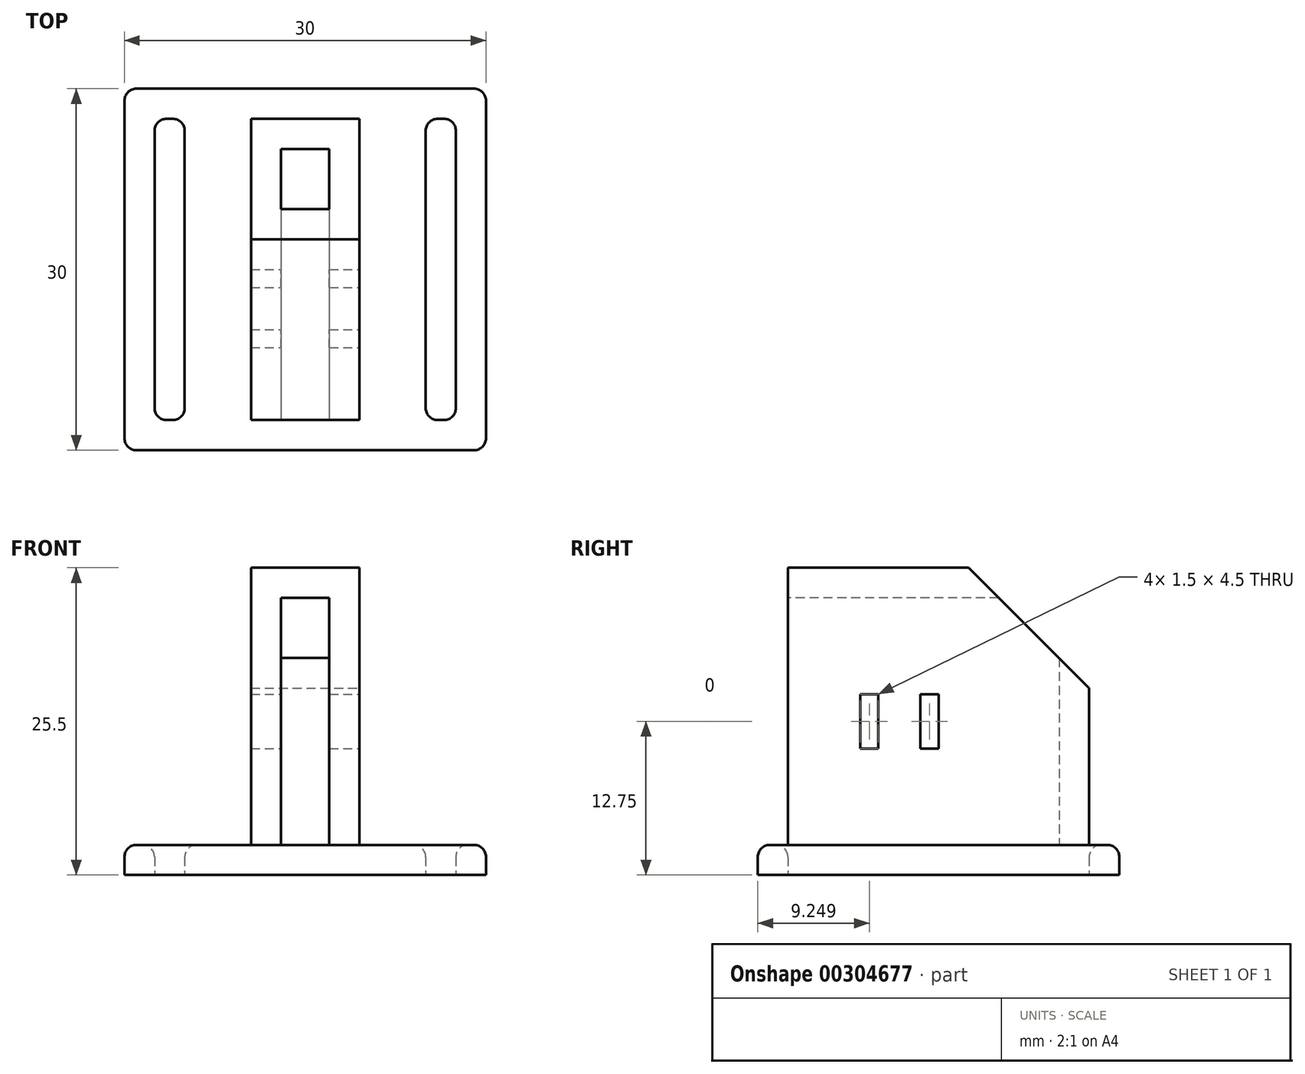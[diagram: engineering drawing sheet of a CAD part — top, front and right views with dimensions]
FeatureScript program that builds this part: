
annotation { "Feature Type Name" : "Feature", "Feature Type Description" : "" }
export const myFeature = defineFeature(function(context is Context, id is Id, definition is map)
    precondition{}
    {
        {
            var Q0;
            Q0=qCreatedBy(makeId("Top.planeOp"),FACE);
            var sketch = newSketch(context, id + "F0", { "sketchPlane" : qUnion([Q0])});
            skLineSegment(sketch, "E0.bottom", {"start": v(-52.92, 47.7) * mm, "end": v(-22.92, 47.7) * mm});
            skLineSegment(sketch, "E0.top", {"start": v(-52.92, 17.7) * mm, "end": v(-22.92, 17.7) * mm});
            skLineSegment(sketch, "E0.left", {"start": v(-52.92, 47.7) * mm, "end": v(-52.92, 17.7) * mm});
            skLineSegment(sketch, "E0.right", {"start": v(-22.92, 47.7) * mm, "end": v(-22.92, 17.7) * mm});
            skLineSegment(sketch, "E1.bottom", {"start": v(-50.42, 45.2) * mm, "end": v(-47.92, 45.2) * mm});
            skLineSegment(sketch, "E1.top", {"start": v(-50.42, 20.2) * mm, "end": v(-47.92, 20.2) * mm});
            skLineSegment(sketch, "E1.left", {"start": v(-50.42, 45.2) * mm, "end": v(-50.42, 20.2) * mm});
            skLineSegment(sketch, "E1.right", {"start": v(-47.92, 45.2) * mm, "end": v(-47.92, 20.2) * mm});
            skLineSegment(sketch, "E2.bottom", {"start": v(-25.42, 45.2) * mm, "end": v(-27.92, 45.2) * mm});
            skLineSegment(sketch, "E2.top", {"start": v(-25.42, 20.2) * mm, "end": v(-27.92, 20.2) * mm});
            skLineSegment(sketch, "E2.left", {"start": v(-25.42, 45.2) * mm, "end": v(-25.42, 20.2) * mm});
            skLineSegment(sketch, "E2.right", {"start": v(-27.92, 45.2) * mm, "end": v(-27.92, 20.2) * mm});
            skSolve(sketch);
        }
        {
            var Q0;
            Q0=makeQuery(id+"F0.imprint","IMPRINT",FACE,{"disambiguationData":[TD([[makeQuery(id+"F0.imprint","IMPRINT",EDGE,{"derivedFrom":sQuery(id+"F0.wireOp",EDGE,"E0.bottom")}),-1.0]])]});
            extrude(context, id + "F1", {"entities" : qUnion([Q0]), "depth" : 2.5 * mm});
        }
        {
            var Q0;
            Q0=makeQuery(id+"F1.opExtrude","CAP_FACE",FACE,{"disambiguationData":[OSD([sQuery(id+"F0.wireOp",EDGE,"E0.bottom"),sQuery(id+"F0.wireOp",EDGE,"E0.top"),sQuery(id+"F0.wireOp",EDGE,"E0.left"),sQuery(id+"F0.wireOp",EDGE,"E0.right"),sQuery(id+"F0.wireOp",EDGE,"E1.bottom"),sQuery(id+"F0.wireOp",EDGE,"E1.top"),sQuery(id+"F0.wireOp",EDGE,"E1.left"),sQuery(id+"F0.wireOp",EDGE,"E1.right"),sQuery(id+"F0.wireOp",EDGE,"E2.bottom"),sQuery(id+"F0.wireOp",EDGE,"E2.top"),sQuery(id+"F0.wireOp",EDGE,"E2.left"),sQuery(id+"F0.wireOp",EDGE,"E2.right")])],"isStart":false});
            var sketch = newSketch(context, id + "F2", { "sketchPlane" : qUnion([Q0])});
            skLineSegment(sketch, "E3.bottom", {"start": v(-33.42, 45.2) * mm, "end": v(-35.92, 45.2) * mm});
            skLineSegment(sketch, "E3.top", {"start": v(-33.42, 20.2) * mm, "end": v(-35.92, 20.2) * mm});
            skLineSegment(sketch, "E3.left", {"start": v(-33.42, 45.2) * mm, "end": v(-33.42, 20.2) * mm});
            skLineSegment(sketch, "E3.right", {"start": v(-35.92, 45.2) * mm, "end": v(-35.92, 20.2) * mm});
            skLineSegment(sketch, "E4.bottom", {"start": v(-42.42, 45.2) * mm, "end": v(-39.92, 45.2) * mm});
            skLineSegment(sketch, "E4.top", {"start": v(-42.42, 20.2) * mm, "end": v(-39.92, 20.2) * mm});
            skLineSegment(sketch, "E4.left", {"start": v(-42.42, 45.2) * mm, "end": v(-42.42, 20.2) * mm});
            skLineSegment(sketch, "E4.right", {"start": v(-39.92, 45.2) * mm, "end": v(-39.92, 20.2) * mm});
            skLineSegment(sketch, "E5.bottom", {"start": v(-39.92, 45.2) * mm, "end": v(-35.92, 45.2) * mm});
            skLineSegment(sketch, "E5.top", {"start": v(-39.92, 42.7) * mm, "end": v(-35.92, 42.7) * mm});
            skLineSegment(sketch, "E5.left", {"start": v(-39.92, 45.2) * mm, "end": v(-39.92, 42.7) * mm});
            skLineSegment(sketch, "E5.right", {"start": v(-35.92, 45.2) * mm, "end": v(-35.92, 42.7) * mm});
            skSolve(sketch);
        }
        {
            var Q0;
            Q0=makeQuery(id+"F2.imprint","IMPRINT",FACE,{"disambiguationData":[TD([[makeQuery(id+"F2.imprint","IMPRINT",EDGE,{"derivedFrom":sQuery(id+"F2.wireOp",EDGE,"E4.bottom")}),-1.0]])]});
            var Q1;
            Q1=makeQuery(id+"F2.imprint","IMPRINT",FACE,{"disambiguationData":[TD([[makeQuery(id+"F2.imprint","IMPRINT",EDGE,{"derivedFrom":sQuery(id+"F2.wireOp",EDGE,"E3.bottom")}),1.0]])]});
            var Q2;
            Q2=makeQuery(id+"F2.imprint","IMPRINT",FACE,{"disambiguationData":[TD([[makeQuery(id+"F2.imprint","IMPRINT",EDGE,{"derivedFrom":sQuery(id+"F2.wireOp",EDGE,"E5.bottom")}),-1.0]])]});
            extrude(context, id + "F3", {"entities" : qUnion([Q0, Q1, Q2]), "depth" : 20.5 * mm});
        }
        {
            var Q0;
            Q0=makeQuery(id+"F3.opExtrude","CAP_FACE",FACE,{"disambiguationData":[OSD([sQuery(id+"F2.wireOp",EDGE,"E3.bottom"),sQuery(id+"F2.wireOp",EDGE,"E3.top"),sQuery(id+"F2.wireOp",EDGE,"E3.left"),sQuery(id+"F2.wireOp",EDGE,"E3.right"),sQuery(id+"F2.wireOp",EDGE,"E4.bottom"),sQuery(id+"F2.wireOp",EDGE,"E4.top"),sQuery(id+"F2.wireOp",EDGE,"E4.left"),sQuery(id+"F2.wireOp",EDGE,"E4.right"),sQuery(id+"F2.wireOp",EDGE,"E5.bottom"),sQuery(id+"F2.wireOp",EDGE,"E5.top")])],"isStart":false});
            var sketch = newSketch(context, id + "F4", { "sketchPlane" : qUnion([Q0])});
            skLineSegment(sketch, "E6.bottom", {"start": v(-42.42, 20.2) * mm, "end": v(-33.42, 20.2) * mm});
            skLineSegment(sketch, "E6.top", {"start": v(-42.42, 45.2) * mm, "end": v(-33.42, 45.2) * mm});
            skLineSegment(sketch, "E6.left", {"start": v(-42.42, 20.2) * mm, "end": v(-42.42, 45.2) * mm});
            skLineSegment(sketch, "E6.right", {"start": v(-33.42, 20.2) * mm, "end": v(-33.42, 45.2) * mm});
            skSolve(sketch);
        }
        {
            var Q0;
            Q0 = qSketchRegion(id + "F4", true);
            extrude(context, id + "F5", {"entities" : qUnion([Q0]), "operationType" : NewBodyOperationType.ADD, "depth" : 2.5 * mm});
        }
        {
            var Q0;
            Q0=makeQuery(id+"F5.boolean.opBoolean","MERGE",FACE,{"derivedFrom":[makeQuery(id+"F3.opExtrude","SWEPT_FACE",FACE,{"disambiguationData":[OSD([sQuery(id+"F2.wireOp",EDGE,"E3.left")])]}),makeQuery(id+"F5.opExtrude","SWEPT_FACE",FACE,{"disambiguationData":[OSD([sQuery(id+"F4.wireOp",EDGE,"E6.right")])]})]});
            var sketch = newSketch(context, id + "F6", { "sketchPlane" : qUnion([Q0])});
            skLineSegment(sketch, "E7.bottom", {"start": v(26.2, 15) * mm, "end": v(27.7, 15) * mm});
            skLineSegment(sketch, "E7.top", {"start": v(26.2, 10.5) * mm, "end": v(27.7, 10.5) * mm});
            skLineSegment(sketch, "E7.left", {"start": v(26.2, 15) * mm, "end": v(26.2, 10.5) * mm});
            skLineSegment(sketch, "E7.right", {"start": v(27.7, 15) * mm, "end": v(27.7, 10.5) * mm});
            skLineSegment(sketch, "E8.bottom", {"start": v(31.2, 15) * mm, "end": v(32.7, 15) * mm});
            skLineSegment(sketch, "E8.top", {"start": v(31.2, 10.5) * mm, "end": v(32.7, 10.5) * mm});
            skLineSegment(sketch, "E8.left", {"start": v(31.2, 15) * mm, "end": v(31.2, 10.5) * mm});
            skLineSegment(sketch, "E8.right", {"start": v(32.7, 15) * mm, "end": v(32.7, 10.5) * mm});
            skLineSegment(sketch, "E9", {"start": v(35.2, 25.5) * mm, "end": v(45.2, 15.5) * mm});
            skLineSegment(sketch, "E10", {"start": v(45.2, 15.5) * mm, "end": v(45.2, 25.5) * mm});
            skLineSegment(sketch, "E11", {"start": v(45.2, 25.5) * mm, "end": v(35.2, 25.5) * mm});
            skSolve(sketch);
        }
        {
            var Q0;
            Q0 = qSketchRegion(id + "F6", true);
            extrude(context, id + "F7", {"entities" : qUnion([Q0]), "operationType" : NewBodyOperationType.REMOVE, "oppositeDirection" : true, "depth" : 25 * mm});
        }
        {
            var Q0;
            Q0=makeQuery(id+"F1.opExtrude","SWEPT_EDGE",EDGE,{"disambiguationData":[OSD([sQuery(id+"F0.wireOp",EDGE,"E0.bottom"),sQuery(id+"F0.wireOp",EDGE,"E0.left")])]});
            var Q1;
            Q1=makeQuery(id+"F1.opExtrude","SWEPT_EDGE",EDGE,{"disambiguationData":[OSD([sQuery(id+"F0.wireOp",EDGE,"E0.top"),sQuery(id+"F0.wireOp",EDGE,"E0.left")])]});
            var Q2;
            Q2=makeQuery(id+"F3.opExtrude","SWEPT_EDGE",EDGE,{"disambiguationData":[OSD([sQuery(id+"F2.wireOp",EDGE,"E4.bottom"),sQuery(id+"F2.wireOp",EDGE,"E4.left")])]});
            var Q3;
            Q3=makeQuery(id+"F3.opExtrude","SWEPT_EDGE",EDGE,{"disambiguationData":[OSD([sQuery(id+"F2.wireOp",EDGE,"E3.bottom"),sQuery(id+"F2.wireOp",EDGE,"E3.left")])]});
            var Q4;
            Q4=makeQuery(id+"F1.opExtrude","SWEPT_EDGE",EDGE,{"disambiguationData":[OSD([sQuery(id+"F0.wireOp",EDGE,"E0.top"),sQuery(id+"F0.wireOp",EDGE,"E0.right")])]});
            var Q5;
            Q5=makeQuery(id+"F1.opExtrude","SWEPT_EDGE",EDGE,{"disambiguationData":[OSD([sQuery(id+"F0.wireOp",EDGE,"E0.bottom"),sQuery(id+"F0.wireOp",EDGE,"E0.right")])]});
            var Q6;
            Q6=makeQuery(id+"F1.opExtrude","SWEPT_EDGE",EDGE,{"disambiguationData":[OSD([sQuery(id+"F0.wireOp",EDGE,"E2.bottom"),sQuery(id+"F0.wireOp",EDGE,"E2.right")])]});
            var Q7;
            Q7=makeQuery(id+"F1.opExtrude","SWEPT_EDGE",EDGE,{"disambiguationData":[OSD([sQuery(id+"F0.wireOp",EDGE,"E1.bottom"),sQuery(id+"F0.wireOp",EDGE,"E1.left")])]});
            var Q8;
            Q8=makeQuery(id+"F1.opExtrude","SWEPT_EDGE",EDGE,{"disambiguationData":[OSD([sQuery(id+"F0.wireOp",EDGE,"E1.top"),sQuery(id+"F0.wireOp",EDGE,"E1.right")])]});
            var Q9;
            Q9=makeQuery(id+"F1.opExtrude","SWEPT_EDGE",EDGE,{"disambiguationData":[OSD([sQuery(id+"F0.wireOp",EDGE,"E2.top"),sQuery(id+"F0.wireOp",EDGE,"E2.right")])]});
            var Q10;
            Q10=makeQuery(id+"F3.opExtrude","SWEPT_EDGE",EDGE,{"disambiguationData":[OSD([sQuery(id+"F2.wireOp",EDGE,"E4.top"),sQuery(id+"F2.wireOp",EDGE,"E4.left")])]});
            var Q11;
            Q11=makeQuery(id+"F3.opExtrude","SWEPT_EDGE",EDGE,{"disambiguationData":[OSD([sQuery(id+"F2.wireOp",EDGE,"E4.top"),sQuery(id+"F2.wireOp",EDGE,"E4.right")])]});
            var Q12;
            Q12=makeQuery(id+"F3.opExtrude","SWEPT_EDGE",EDGE,{"disambiguationData":[OSD([sQuery(id+"F2.wireOp",EDGE,"E3.top"),sQuery(id+"F2.wireOp",EDGE,"E3.left")])]});
            var Q13;
            Q13=makeQuery(id+"F3.opExtrude","SWEPT_EDGE",EDGE,{"disambiguationData":[OSD([sQuery(id+"F2.wireOp",EDGE,"E3.top"),sQuery(id+"F2.wireOp",EDGE,"E3.right")])]});
            var Q14;
            Q14=makeQuery(id+"F3.opExtrude","SWEPT_EDGE",EDGE,{"disambiguationData":[OSD([sQuery(id+"F2.wireOp",EDGE,"E4.right"),sQuery(id+"F2.wireOp",EDGE,"E5.top"),sQuery(id+"F2.wireOp",EDGE,"E5.left")])]});
            var Q15;
            Q15=makeQuery(id+"F3.opExtrude","SWEPT_EDGE",EDGE,{"disambiguationData":[OSD([sQuery(id+"F2.wireOp",EDGE,"E3.right"),sQuery(id+"F2.wireOp",EDGE,"E5.top"),sQuery(id+"F2.wireOp",EDGE,"E5.right")])]});
            var Q16;
            Q16=makeQuery(id+"F1.opExtrude","SWEPT_EDGE",EDGE,{"disambiguationData":[OSD([sQuery(id+"F0.wireOp",EDGE,"E2.bottom"),sQuery(id+"F0.wireOp",EDGE,"E2.left")])]});
            var Q17;
            Q17=makeQuery(id+"F1.opExtrude","SWEPT_EDGE",EDGE,{"disambiguationData":[OSD([sQuery(id+"F0.wireOp",EDGE,"E1.bottom"),sQuery(id+"F0.wireOp",EDGE,"E1.right")])]});
            var Q18;
            Q18=makeQuery(id+"F1.opExtrude","SWEPT_EDGE",EDGE,{"disambiguationData":[OSD([sQuery(id+"F0.wireOp",EDGE,"E1.top"),sQuery(id+"F0.wireOp",EDGE,"E1.left")])]});
            var Q19;
            Q19=makeQuery(id+"F1.opExtrude","SWEPT_EDGE",EDGE,{"disambiguationData":[OSD([sQuery(id+"F0.wireOp",EDGE,"E2.top"),sQuery(id+"F0.wireOp",EDGE,"E2.left")])]});
            var Q20;
            Q20=makeQuery(id+"F3.opExtrude","CAP_EDGE",EDGE,{"disambiguationData":[OSD([sQuery(id+"F2.wireOp",EDGE,"E3.left")])],"isStart":true});
            var Q21;
            Q21=makeQuery(id+"F5.opExtrude","CAP_EDGE",EDGE,{"disambiguationData":[OSD([sQuery(id+"F4.wireOp",EDGE,"E6.bottom")])],"isStart":false});
            var Q22;
            Q22=makeQuery(id+"F5.opExtrude","CAP_EDGE",EDGE,{"disambiguationData":[OSD([sQuery(id+"F4.wireOp",EDGE,"E6.left")])],"isStart":false});
            var Q23;
            Q23=makeQuery(id+"F5.opExtrude","CAP_EDGE",EDGE,{"disambiguationData":[OSD([sQuery(id+"F4.wireOp",EDGE,"E6.right")])],"isStart":false});
            var Q24;
            Q24=makeQuery(id+"F5.opExtrude","CAP_EDGE",EDGE,{"disambiguationData":[OSD([sQuery(id+"F4.wireOp",EDGE,"E6.top")])],"isStart":false});
            var Q25;
            Q25=makeQuery(id+"F5.opExtrude","CAP_EDGE",EDGE,{"disambiguationData":[OSD([sQuery(id+"F4.wireOp",EDGE,"E6.bottom")])],"isStart":true});
            var Q26;
            Q26=makeQuery(id+"F7.boolean.opBoolean","COPY",EDGE,{"derivedFrom":makeQuery(id+"F7.opExtrude","SWEPT_EDGE",EDGE,{"disambiguationData":[OSD([sQuery(id+"F2.wireOp",EDGE,"E3.bottom"),sQuery(id+"F2.wireOp",EDGE,"E3.left"),sQuery(id+"F4.wireOp",EDGE,"E6.top"),sQuery(id+"F4.wireOp",EDGE,"E6.right"),sQuery(id+"F6.wireOp",EDGE,"E9"),sQuery(id+"F6.wireOp",EDGE,"E10")])]})});
            var Q27;
            Q27=makeQuery(id+"F7.boolean.opBoolean","COPY",EDGE,{"derivedFrom":makeQuery(id+"F7.opExtrude","CAP_EDGE",EDGE,{"disambiguationData":[OSD([sQuery(id+"F6.wireOp",EDGE,"E9")])],"isStart":true})});
            var Q28;
            Q28=makeQuery(id+"F7.boolean.opBoolean","COPY",EDGE,{"derivedFrom":makeQuery(id+"F7.opExtrude","SWEPT_EDGE",EDGE,{"disambiguationData":[OSD([sQuery(id+"F4.wireOp",EDGE,"E6.right"),sQuery(id+"F6.wireOp",EDGE,"E9"),sQuery(id+"F6.wireOp",EDGE,"E11")])]})});
            var Q29;
            Q29=makeQuery(id+"F7.boolean.opBoolean","INTERSECT",EDGE,{"derivedFrom":[makeQuery(id+"F5.boolean.opBoolean","MERGE",FACE,{"derivedFrom":[makeQuery(id+"F3.opExtrude","SWEPT_FACE",FACE,{"disambiguationData":[OSD([sQuery(id+"F2.wireOp",EDGE,"E4.left")])]}),makeQuery(id+"F5.opExtrude","SWEPT_FACE",FACE,{"disambiguationData":[OSD([sQuery(id+"F4.wireOp",EDGE,"E6.left")])]})]}),makeQuery(id+"F7.opExtrude","SWEPT_FACE",FACE,{"disambiguationData":[OSD([sQuery(id+"F6.wireOp",EDGE,"E9")])]})]});
            var Q30;
            Q30=makeQuery(id+"F7.boolean.opBoolean","COPY",EDGE,{"derivedFrom":makeQuery(id+"F7.opExtrude","CAP_EDGE",EDGE,{"disambiguationData":[OSD([sQuery(id+"F6.wireOp",EDGE,"E7.left")])],"isStart":true})});
            var Q31;
            Q31=makeQuery(id+"F7.boolean.opBoolean","INTERSECT",EDGE,{"derivedFrom":[makeQuery(id+"F3.opExtrude","SWEPT_FACE",FACE,{"disambiguationData":[OSD([sQuery(id+"F2.wireOp",EDGE,"E3.right")])]}),makeQuery(id+"F7.opExtrude","SWEPT_FACE",FACE,{"disambiguationData":[OSD([sQuery(id+"F6.wireOp",EDGE,"E7.left")])]})]});
            var Q32;
            Q32=makeQuery(id+"F7.boolean.opBoolean","COPY",EDGE,{"derivedFrom":makeQuery(id+"F7.opExtrude","CAP_EDGE",EDGE,{"disambiguationData":[OSD([sQuery(id+"F6.wireOp",EDGE,"E8.left")])],"isStart":true})});
            var Q33;
            Q33=makeQuery(id+"F7.boolean.opBoolean","COPY",EDGE,{"derivedFrom":makeQuery(id+"F7.opExtrude","CAP_EDGE",EDGE,{"disambiguationData":[OSD([sQuery(id+"F6.wireOp",EDGE,"E8.right")])],"isStart":true})});
            var Q34;
            Q34=makeQuery(id+"F7.boolean.opBoolean","COPY",EDGE,{"derivedFrom":makeQuery(id+"F7.opExtrude","CAP_EDGE",EDGE,{"disambiguationData":[OSD([sQuery(id+"F6.wireOp",EDGE,"E7.right")])],"isStart":true})});
            var Q35;
            Q35=makeQuery(id+"F7.boolean.opBoolean","INTERSECT",EDGE,{"derivedFrom":[makeQuery(id+"F5.boolean.opBoolean","MERGE",FACE,{"derivedFrom":[makeQuery(id+"F3.opExtrude","SWEPT_FACE",FACE,{"disambiguationData":[OSD([sQuery(id+"F2.wireOp",EDGE,"E4.left")])]}),makeQuery(id+"F5.opExtrude","SWEPT_FACE",FACE,{"disambiguationData":[OSD([sQuery(id+"F4.wireOp",EDGE,"E6.left")])]})]}),makeQuery(id+"F7.opExtrude","SWEPT_FACE",FACE,{"disambiguationData":[OSD([sQuery(id+"F6.wireOp",EDGE,"E8.right")])]})]});
            var Q36;
            Q36=makeQuery(id+"F7.boolean.opBoolean","INTERSECT",EDGE,{"derivedFrom":[makeQuery(id+"F3.opExtrude","SWEPT_FACE",FACE,{"disambiguationData":[OSD([sQuery(id+"F2.wireOp",EDGE,"E4.right")])]}),makeQuery(id+"F7.opExtrude","SWEPT_FACE",FACE,{"disambiguationData":[OSD([sQuery(id+"F6.wireOp",EDGE,"E8.right")])]})]});
            var Q37;
            Q37=makeQuery(id+"F7.boolean.opBoolean","INTERSECT",EDGE,{"derivedFrom":[makeQuery(id+"F5.boolean.opBoolean","MERGE",FACE,{"derivedFrom":[makeQuery(id+"F3.opExtrude","SWEPT_FACE",FACE,{"disambiguationData":[OSD([sQuery(id+"F2.wireOp",EDGE,"E4.left")])]}),makeQuery(id+"F5.opExtrude","SWEPT_FACE",FACE,{"disambiguationData":[OSD([sQuery(id+"F4.wireOp",EDGE,"E6.left")])]})]}),makeQuery(id+"F7.opExtrude","SWEPT_FACE",FACE,{"disambiguationData":[OSD([sQuery(id+"F6.wireOp",EDGE,"E8.left")])]})]});
            var Q38;
            Q38=makeQuery(id+"F7.boolean.opBoolean","INTERSECT",EDGE,{"derivedFrom":[makeQuery(id+"F5.boolean.opBoolean","MERGE",FACE,{"derivedFrom":[makeQuery(id+"F3.opExtrude","SWEPT_FACE",FACE,{"disambiguationData":[OSD([sQuery(id+"F2.wireOp",EDGE,"E4.left")])]}),makeQuery(id+"F5.opExtrude","SWEPT_FACE",FACE,{"disambiguationData":[OSD([sQuery(id+"F4.wireOp",EDGE,"E6.left")])]})]}),makeQuery(id+"F7.opExtrude","SWEPT_FACE",FACE,{"disambiguationData":[OSD([sQuery(id+"F6.wireOp",EDGE,"E7.right")])]})]});
            var Q39;
            Q39=makeQuery(id+"F7.boolean.opBoolean","INTERSECT",EDGE,{"derivedFrom":[makeQuery(id+"F3.opExtrude","SWEPT_FACE",FACE,{"disambiguationData":[OSD([sQuery(id+"F2.wireOp",EDGE,"E4.right")])]}),makeQuery(id+"F7.opExtrude","SWEPT_FACE",FACE,{"disambiguationData":[OSD([sQuery(id+"F6.wireOp",EDGE,"E7.right")])]})]});
            var Q40;
            Q40=makeQuery(id+"F7.boolean.opBoolean","INTERSECT",EDGE,{"derivedFrom":[makeQuery(id+"F5.boolean.opBoolean","MERGE",FACE,{"derivedFrom":[makeQuery(id+"F3.opExtrude","SWEPT_FACE",FACE,{"disambiguationData":[OSD([sQuery(id+"F2.wireOp",EDGE,"E4.left")])]}),makeQuery(id+"F5.opExtrude","SWEPT_FACE",FACE,{"disambiguationData":[OSD([sQuery(id+"F4.wireOp",EDGE,"E6.left")])]})]}),makeQuery(id+"F7.opExtrude","SWEPT_FACE",FACE,{"disambiguationData":[OSD([sQuery(id+"F6.wireOp",EDGE,"E7.left")])]})]});
            var Q41;
            Q41=makeQuery(id+"F7.boolean.opBoolean","INTERSECT",EDGE,{"derivedFrom":[makeQuery(id+"F3.opExtrude","SWEPT_FACE",FACE,{"disambiguationData":[OSD([sQuery(id+"F2.wireOp",EDGE,"E3.right")])]}),makeQuery(id+"F7.opExtrude","SWEPT_FACE",FACE,{"disambiguationData":[OSD([sQuery(id+"F6.wireOp",EDGE,"E8.left")])]})]});
            var Q42;
            Q42=makeQuery(id+"F3.opExtrude","SWEPT_FACE",FACE,{"disambiguationData":[OSD([sQuery(id+"F2.wireOp",EDGE,"E4.right")])]});
            var Q43;
            Q43=makeQuery(id+"F5.boolean.opBoolean","MERGE",FACE,{"derivedFrom":[makeQuery(id+"F3.opExtrude","SWEPT_FACE",FACE,{"disambiguationData":[OSD([sQuery(id+"F2.wireOp",EDGE,"E3.left")])]}),makeQuery(id+"F5.opExtrude","SWEPT_FACE",FACE,{"disambiguationData":[OSD([sQuery(id+"F4.wireOp",EDGE,"E6.right")])]})]});
            var Q44;
            Q44=makeQuery(id+"F5.boolean.opBoolean","MERGE",FACE,{"derivedFrom":[makeQuery(id+"F3.opExtrude","SWEPT_FACE",FACE,{"disambiguationData":[OSD([sQuery(id+"F2.wireOp",EDGE,"E4.left")])]}),makeQuery(id+"F5.opExtrude","SWEPT_FACE",FACE,{"disambiguationData":[OSD([sQuery(id+"F4.wireOp",EDGE,"E6.left")])]})]});
            var Q45;
            Q45=makeQuery(id+"F3.opExtrude","SWEPT_FACE",FACE,{"disambiguationData":[OSD([sQuery(id+"F2.wireOp",EDGE,"E3.right")])]});
            var Q46;
            Q46=makeQuery(id+"F1.opExtrude","CAP_FACE",FACE,{"disambiguationData":[OSD([sQuery(id+"F0.wireOp",EDGE,"E0.bottom"),sQuery(id+"F0.wireOp",EDGE,"E0.top"),sQuery(id+"F0.wireOp",EDGE,"E0.left"),sQuery(id+"F0.wireOp",EDGE,"E0.right"),sQuery(id+"F0.wireOp",EDGE,"E1.bottom"),sQuery(id+"F0.wireOp",EDGE,"E1.top"),sQuery(id+"F0.wireOp",EDGE,"E1.left"),sQuery(id+"F0.wireOp",EDGE,"E1.right"),sQuery(id+"F0.wireOp",EDGE,"E2.bottom"),sQuery(id+"F0.wireOp",EDGE,"E2.top"),sQuery(id+"F0.wireOp",EDGE,"E2.left"),sQuery(id+"F0.wireOp",EDGE,"E2.right")])],"isStart":false});
            fillet(context, id + "F8", {"entities" : qUnion([Q0, Q1, Q2, Q3, Q4, Q5, Q6, Q7, Q8, Q9, Q10, Q11, Q12, Q13, Q14, Q15, Q16, Q17, Q18, Q19, Q20, Q21, Q22, Q23, Q24, Q25, Q26, Q27, Q28, Q29, Q30, Q31, Q32, Q33, Q34, Q35, Q36, Q37, Q38, Q39, Q40, Q41, Q42, Q43, Q44, Q45, Q46]), "radius" : 1 * mm, "tangentPropagation" : true, "allowEdgeOverflow" : false});
        }
    });
